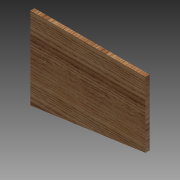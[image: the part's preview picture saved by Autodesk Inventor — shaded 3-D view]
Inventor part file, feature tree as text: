
AUTODESK INVENTOR PART (.ipt)
format: ipt  version: 2012 (Build 160160000, 160)  size: 94,208 bytes
history: native  units: in
note: dims shown in document units (in); Inventor stores cm internally (conversion verified against a paired STEP export)
features: extrude x1, sketch x1
ambient origin geometry x8: Origin, YZ Plane, XZ Plane, XY Plane, X Axis, Y Axis, Z Axis, Center Point
bodies: Solid1 (feature_tree)
feature tree (2):
  extrude  "Extrusion1"  Depth=4.0in
  sketch  "Sketch1"  dims[d0=7.0in d1=4.0in d2=0.25in d3=0.0in d4=1.0in]
